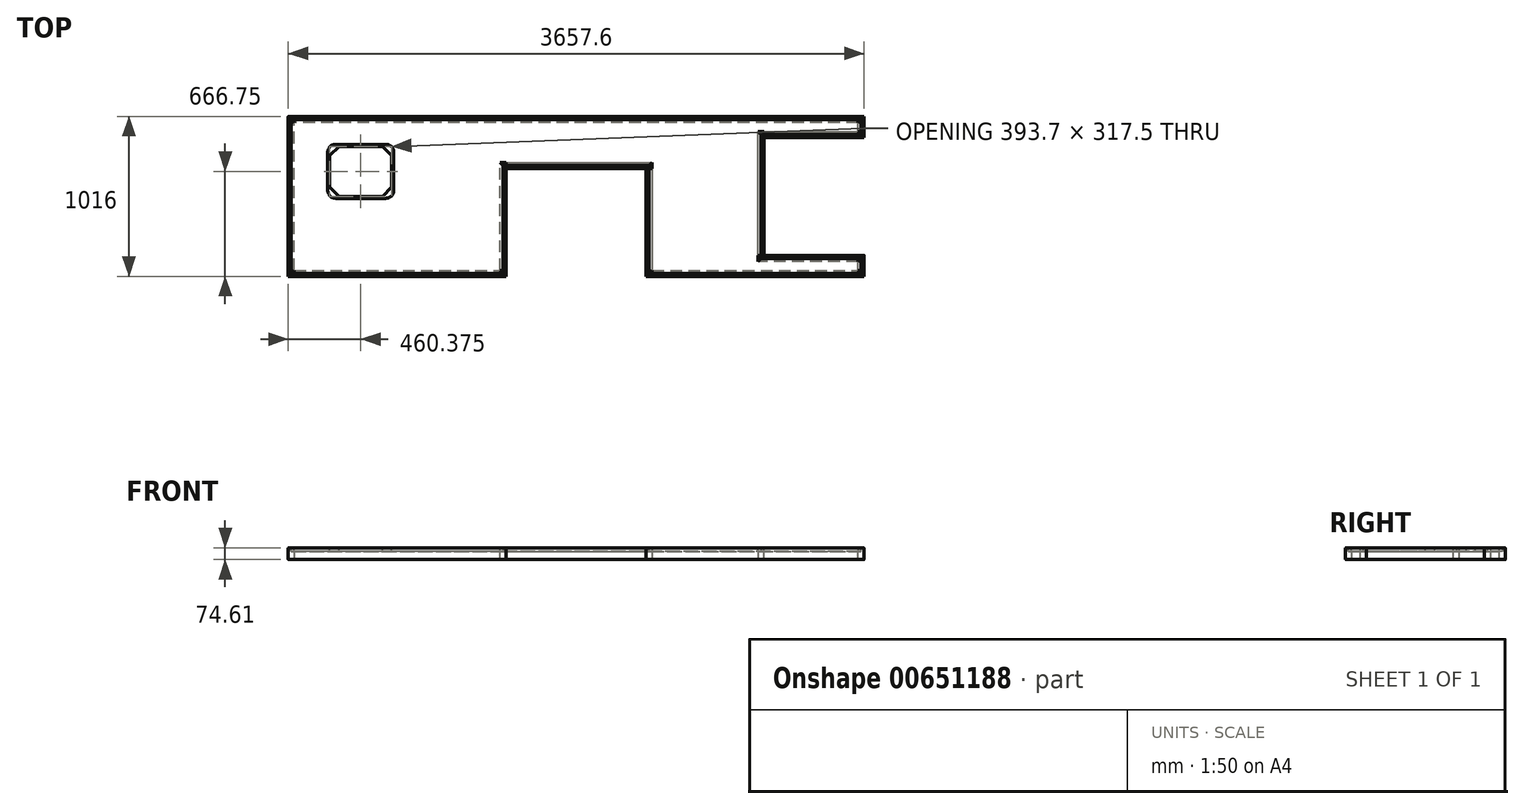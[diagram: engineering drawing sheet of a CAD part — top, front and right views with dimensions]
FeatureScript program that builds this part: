
annotation { "Feature Type Name" : "Feature", "Feature Type Description" : "" }
export const myFeature = defineFeature(function(context is Context, id is Id, definition is map)
    precondition{}
    {
        {
            var Q0;
            Q0=qCreatedBy(makeId("Top.planeOp"),FACE);
            var sketch = newSketch(context, id + "F0", { "sketchPlane" : qUnion([Q0])});
            skLineSegment(sketch, "E0.bottom", {"start": v(1809.75, 488.95) * mm, "end": v(-1809.75, 488.95) * mm});
            skLineSegment(sketch, "E0.top", {"start": v(1809.75, -488.95) * mm, "end": v(463.55, -488.95) * mm});
            skLineSegment(sketch, "E0.left", {"start": v(1809.75, 488.95) * mm, "end": v(1809.75, 393.7) * mm});
            skLineSegment(sketch, "E0.right", {"start": v(-1809.75, 488.95) * mm, "end": v(-1809.75, -488.95) * mm});
            skPoint(sketch, "E0.middle", {"position": v(0, 0) * mm});
            skLineSegment(sketch, "E1", {"start": v(-463.55, -488.95) * mm, "end": v(-463.55, 196.85) * mm});
            skLineSegment(sketch, "E2", {"start": v(-463.55, 196.85) * mm, "end": v(463.55, 196.85) * mm});
            skLineSegment(sketch, "E3", {"start": v(463.55, 196.85) * mm, "end": v(463.55, -488.95) * mm});
            skLineSegment(sketch, "E4.trimOffspring", {"start": v(-463.55, -488.95) * mm, "end": v(-1809.75, -488.95) * mm});
            skLineSegment(sketch, "E5", {"start": v(1809.75, 393.7) * mm, "end": v(1174.75, 393.7) * mm});
            skLineSegment(sketch, "E6", {"start": v(1174.75, 393.7) * mm, "end": v(1174.75, -393.7) * mm});
            skLineSegment(sketch, "E7", {"start": v(1174.75, -393.7) * mm, "end": v(1809.75, -393.7) * mm});
            skLineSegment(sketch, "E8.trimOffspring", {"start": v(1809.75, -393.7) * mm, "end": v(1809.75, -488.95) * mm});
            skSolve(sketch);
        }
        {
            var Q0;
            Q0=makeQuery(id+"F0.imprint","IMPRINT",FACE,{"disambiguationData":[TD([[makeQuery(id+"F0.imprint","IMPRINT",EDGE,{"derivedFrom":sQuery(id+"F0.wireOp",EDGE,"E0.bottom")}),1.0]])]});
            extrude(context, id + "F1", {"entities" : qUnion([Q0]), "oppositeDirection" : true, "depth" : 23.8 * mm, "offsetDistance" : 25.4 * mm});
        }
        {
            var Q0;
            Q0=qCreatedBy(makeId("Top.planeOp"),FACE);
            var sketch = newSketch(context, id + "F2", { "sketchPlane" : qUnion([Q0])});
            skLineSegment(sketch, "E9.bottom", {"start": v(-1209.68, 330.2) * mm, "end": v(-1527.18, 330.2) * mm});
            skLineSegment(sketch, "E9.top", {"start": v(-1209.68, -12.7) * mm, "end": v(-1527.18, -12.7) * mm});
            skLineSegment(sketch, "E9.left", {"start": v(-1158.88, 279.4) * mm, "end": v(-1158.88, 38.1) * mm});
            skLineSegment(sketch, "E9.right", {"start": v(-1577.98, 279.4) * mm, "end": v(-1577.98, 38.1) * mm});
            skPoint(sketch, "E10.visualSharp", {"position": v(-1577.98, 330.2) * mm});
            skArc(sketch, "E10.filletArc", {"start": v(-1527.18, 330.2) * mm, "mid": v(-1563.1, 315.32) * mm, "end": v(-1577.98, 279.4) * mm});
            skPoint(sketch, "E11.visualSharp", {"position": v(-1158.88, 330.2) * mm});
            skArc(sketch, "E11.filletArc", {"start": v(-1158.88, 279.4) * mm, "mid": v(-1173.75, 315.32) * mm, "end": v(-1209.68, 330.2) * mm});
            skPoint(sketch, "E12.visualSharp", {"position": v(-1158.88, -12.7) * mm});
            skArc(sketch, "E12.filletArc", {"start": v(-1209.68, -12.7) * mm, "mid": v(-1173.75, 2.18) * mm, "end": v(-1158.88, 38.1) * mm});
            skPoint(sketch, "E13.visualSharp", {"position": v(-1577.98, -12.7) * mm});
            skArc(sketch, "E13.filletArc", {"start": v(-1577.98, 38.1) * mm, "mid": v(-1563.1, 2.18) * mm, "end": v(-1527.18, -12.7) * mm});
            skSolve(sketch);
        }
        {
            var Q0;
            Q0=makeQuery(id+"F2.imprint","IMPRINT",FACE,{"disambiguationData":[TD([[makeQuery(id+"F2.imprint","IMPRINT",EDGE,{"derivedFrom":sQuery(id+"F2.wireOp",EDGE,"E9.bottom")}),1.0]])]});
            extrude(context, id + "F3", {"entities" : qUnion([Q0]), "operationType" : NewBodyOperationType.REMOVE, "oppositeDirection" : true, "depth" : 3 / 203.2 * mm, "offsetDistance" : 25.4 * mm});
        }
        {
            var Q0;
            Q0=qCreatedBy(makeId("Top.planeOp"),FACE);
            var sketch = newSketch(context, id + "F4", { "sketchPlane" : qUnion([Q0])});
            skPoint(sketch, "E14.0", {"position": v(-1173.75, 315.32) * mm});
            skPoint(sketch, "E15.0", {"position": v(-1158.88, 158.75) * mm});
            skPoint(sketch, "E16.0", {"position": v(-1173.75, 2.18) * mm});
            skPoint(sketch, "E17.0", {"position": v(-1368.43, -12.7) * mm});
            skPoint(sketch, "E18.0", {"position": v(-1563.1, 2.18) * mm});
            skPoint(sketch, "E19.0", {"position": v(-1577.98, 158.75) * mm});
            skPoint(sketch, "E20.0", {"position": v(-1563.1, 315.32) * mm});
            skPoint(sketch, "E21.0", {"position": v(-1368.43, 330.2) * mm});
            skLineSegment(sketch, "E22", {"start": v(-1158.88, 158.75) * mm, "end": v(-1577.98, 158.75) * mm, "construction": true});
            skLineSegment(sketch, "E23", {"start": v(-1368.43, 330.2) * mm, "end": v(-1368.43, -12.7) * mm, "construction": true});
            skLineSegment(sketch, "E24", {"start": v(-1171.58, 158.75) * mm, "end": v(-1171.58, 259.26) * mm});
            skLineSegment(sketch, "E25", {"start": v(-1171.58, 259.26) * mm, "end": v(-1229.81, 317.5) * mm});
            skLineSegment(sketch, "E26", {"start": v(-1229.81, 317.5) * mm, "end": v(-1368.43, 317.5) * mm});
            skLineSegment(sketch, "E27.MirrorCS", {"start": v(-1171.58, 158.75) * mm, "end": v(-1171.58, 58.24) * mm});
            skLineSegment(sketch, "E28.MirrorCS", {"start": v(-1171.58, 58.24) * mm, "end": v(-1229.81, 0) * mm});
            skLineSegment(sketch, "E29.MirrorCS", {"start": v(-1229.81, 0) * mm, "end": v(-1368.43, 0) * mm});
            skLineSegment(sketch, "E30.MirrorCS", {"start": v(-1507.04, 0) * mm, "end": v(-1368.43, 0) * mm});
            skLineSegment(sketch, "E31.MirrorCS", {"start": v(-1565.28, 58.24) * mm, "end": v(-1507.04, 0) * mm});
            skLineSegment(sketch, "E32.MirrorCS", {"start": v(-1565.28, 158.75) * mm, "end": v(-1565.28, 58.24) * mm});
            skLineSegment(sketch, "E33.MirrorCS", {"start": v(-1565.28, 158.75) * mm, "end": v(-1565.28, 259.26) * mm});
            skLineSegment(sketch, "E34.MirrorCS", {"start": v(-1565.28, 259.26) * mm, "end": v(-1507.04, 317.5) * mm});
            skLineSegment(sketch, "E35.MirrorCS", {"start": v(-1507.04, 317.5) * mm, "end": v(-1368.43, 317.5) * mm});
            skSolve(sketch);
        }
        {
            var Q0;
            Q0=makeQuery(id+"F4.imprint","IMPRINT",FACE,{"disambiguationData":[TD([[makeQuery(id+"F4.imprint","IMPRINT",EDGE,{"derivedFrom":sQuery(id+"F4.wireOp",EDGE,"E24")}),1.0]])]});
            extrude(context, id + "F5", {"entities" : qUnion([Q0]), "operationType" : NewBodyOperationType.REMOVE, "endBound" : BoundingType.THROUGH_ALL, "oppositeDirection" : true, "depth" : 25.4 * mm, "offsetDistance" : 25.4 * mm});
        }
        {
            var Q0;
            Q0=qCreatedBy(makeId("Front.planeOp"),FACE);
            var sketch = newSketch(context, id + "F6", { "sketchPlane" : qUnion([Q0])});
            skPoint(sketch, "E36.0", {"position": v(-1809.75, 0) * mm});
            skPoint(sketch, "E37.0", {"position": v(-1809.75, -23.81) * mm});
            skLineSegment(sketch, "E38.0", {"start": v(-1790.7, -23.81) * mm, "end": v(-1809.75, -23.81) * mm});
            skLineSegment(sketch, "E39", {"start": v(-1809.75, 0) * mm, "end": v(-1825.63, 0) * mm});
            skLineSegment(sketch, "E40", {"start": v(-1828.8, -3.17) * mm, "end": v(-1828.8, -71.44) * mm});
            skLineSegment(sketch, "E41", {"start": v(-1825.63, -74.61) * mm, "end": v(-1793.88, -74.61) * mm});
            skLineSegment(sketch, "E42", {"start": v(-1790.7, -71.44) * mm, "end": v(-1790.7, -23.81) * mm});
            skLineSegment(sketch, "E43", {"start": v(-1809.75, 0) * mm, "end": v(-1809.75, -23.81) * mm});
            skPoint(sketch, "E44.visualSharp", {"position": v(-1828.8, 0) * mm});
            skArc(sketch, "E44.filletArc", {"start": v(-1825.63, 0) * mm, "mid": v(-1827.87, -0.93) * mm, "end": v(-1828.8, -3.17) * mm});
            skPoint(sketch, "E45.visualSharp", {"position": v(-1828.8, -74.61) * mm});
            skArc(sketch, "E45.filletArc", {"start": v(-1828.8, -71.44) * mm, "mid": v(-1827.87, -73.68) * mm, "end": v(-1825.63, -74.61) * mm});
            skPoint(sketch, "E46.visualSharp", {"position": v(-1790.7, -74.61) * mm});
            skArc(sketch, "E46.filletArc", {"start": v(-1793.88, -74.61) * mm, "mid": v(-1791.63, -73.68) * mm, "end": v(-1790.7, -71.44) * mm});
            skSolve(sketch);
        }
        {
            var Q0;
            Q0 = qSketchRegion(id + "F6", true);
            extrude(context, id + "F7", {"entities" : qUnion([Q0]), "depth" : 1016 * mm, "offsetDistance" : 25.4 * mm, "symmetric" : true});
        }
        {
            var Q0;
            Q0=qCreatedBy(makeId("Top.planeOp"),FACE);
            var sketch = newSketch(context, id + "F8", { "sketchPlane" : qUnion([Q0])});
            skPoint(sketch, "E47.0", {"position": v(-1828.8, 508) * mm});
            skPoint(sketch, "E48.0", {"position": v(-1790.7, 508) * mm});
            skLineSegment(sketch, "E49", {"start": v(-1828.8, 508) * mm, "end": v(-1790.7, 508) * mm});
            skLineSegment(sketch, "E50", {"start": v(-1790.7, 469.9) * mm, "end": v(-1828.8, 508) * mm});
            skPoint(sketch, "E51.0", {"position": v(-1828.8, -508) * mm});
            skPoint(sketch, "E52.0", {"position": v(-1790.7, -508) * mm});
            skLineSegment(sketch, "E53", {"start": v(-1828.8, -508) * mm, "end": v(-1790.7, -508) * mm});
            skLineSegment(sketch, "E54", {"start": v(-1790.7, -469.9) * mm, "end": v(-1828.8, -508) * mm});
            skLineSegment(sketch, "E55", {"start": v(-1790.7, 508) * mm, "end": v(-1790.7, 469.9) * mm});
            skLineSegment(sketch, "E56", {"start": v(-1790.7, -469.9) * mm, "end": v(-1790.7, -508) * mm});
            skSolve(sketch);
        }
        {
            var Q0;
            Q0 = qSketchRegion(id + "F8", true);
            extrude(context, id + "F9", {"entities" : qUnion([Q0]), "operationType" : NewBodyOperationType.REMOVE, "endBound" : BoundingType.THROUGH_ALL, "oppositeDirection" : true, "depth" : 25.4 * mm, "offsetDistance" : 25.4 * mm});
        }
        {
            var Q0;
            Q0=makeQuery(id+"F1.opExtrude","SWEPT_FACE",FACE,{"disambiguationData":[OSD([sQuery(id+"F0.wireOp",EDGE,"E1")])]});
            var sketch = newSketch(context, id + "F10", { "sketchPlane" : qUnion([Q0])});
            skLineSegment(sketch, "E57.0", {"start": v(-488.95, -23.81) * mm, "end": v(-488.95, 0) * mm});
            skLineSegment(sketch, "E58.0", {"start": v(-469.9, -23.81) * mm, "end": v(-488.95, -23.81) * mm});
            skLineSegment(sketch, "E59", {"start": v(-488.95, 0) * mm, "end": v(-504.83, 0) * mm});
            skLineSegment(sketch, "E60", {"start": v(-508, -3.17) * mm, "end": v(-508, -71.44) * mm});
            skLineSegment(sketch, "E61", {"start": v(-504.83, -74.61) * mm, "end": v(-473.08, -74.61) * mm});
            skLineSegment(sketch, "E62", {"start": v(-469.9, -71.44) * mm, "end": v(-469.9, -23.81) * mm});
            skPoint(sketch, "E63.visualSharp", {"position": v(-508, 0) * mm});
            skArc(sketch, "E63.filletArc", {"start": v(-504.83, 0) * mm, "mid": v(-507.07, -0.93) * mm, "end": v(-508, -3.18) * mm});
            skPoint(sketch, "E64.visualSharp", {"position": v(-508, -74.61) * mm});
            skArc(sketch, "E64.filletArc", {"start": v(-508, -71.44) * mm, "mid": v(-507.07, -73.68) * mm, "end": v(-504.83, -74.61) * mm});
            skPoint(sketch, "E65.visualSharp", {"position": v(-469.9, -74.61) * mm});
            skArc(sketch, "E65.filletArc", {"start": v(-473.08, -74.61) * mm, "mid": v(-470.83, -73.68) * mm, "end": v(-469.9, -71.44) * mm});
            skSolve(sketch);
        }
        {
            var Q0;
            Q0 = qSketchRegion(id + "F10", true);
            extrude(context, id + "F11", {"entities" : qUnion([Q0]), "endBound" : BoundingType.UP_TO_NEXT, "oppositeDirection" : true, "depth" : 25.4 * mm, "offsetDistance" : 25.4 * mm, "hasSecondDirection" : true, "secondDirectionOppositeDirection" : false, "secondDirectionDepth" : 19.05 * mm});
        }
        {
            var Q0;
            Q0=qCreatedBy(makeId("Top.planeOp"),FACE);
            var sketch = newSketch(context, id + "F12", { "sketchPlane" : qUnion([Q0])});
            skPoint(sketch, "E66.0", {"position": v(-444.5, -508) * mm});
            skPoint(sketch, "E67.0", {"position": v(-444.5, -469.9) * mm});
            skLineSegment(sketch, "E68", {"start": v(-444.5, -508) * mm, "end": v(-444.5, -469.9) * mm});
            skLineSegment(sketch, "E69", {"start": v(-444.5, -469.9) * mm, "end": v(-482.6, -469.9) * mm});
            skLineSegment(sketch, "E70", {"start": v(-482.6, -469.9) * mm, "end": v(-444.5, -508) * mm});
            skSolve(sketch);
        }
        {
            var Q0;
            Q0 = qSketchRegion(id + "F12", true);
            extrude(context, id + "F13", {"entities" : qUnion([Q0]), "operationType" : NewBodyOperationType.REMOVE, "endBound" : BoundingType.THROUGH_ALL, "oppositeDirection" : true, "depth" : 25.4 * mm, "offsetDistance" : 25.4 * mm});
        }
        {
            var Q0;
            Q0=makeQuery(id+"F1.opExtrude","SWEPT_FACE",FACE,{"disambiguationData":[OSD([sQuery(id+"F0.wireOp",EDGE,"E2")])]});
            var sketch = newSketch(context, id + "F14", { "sketchPlane" : qUnion([Q0])});
            skLineSegment(sketch, "E71.0", {"start": v(-463.55, -23.81) * mm, "end": v(-463.55, 0) * mm});
            skLineSegment(sketch, "E72", {"start": v(-463.55, 0) * mm, "end": v(-447.68, 0) * mm});
            skLineSegment(sketch, "E73", {"start": v(-444.5, -3.17) * mm, "end": v(-444.5, -71.44) * mm});
            skLineSegment(sketch, "E74", {"start": v(-447.68, -74.61) * mm, "end": v(-479.43, -74.61) * mm});
            skLineSegment(sketch, "E75", {"start": v(-463.55, -23.81) * mm, "end": v(-482.6, -23.81) * mm});
            skLineSegment(sketch, "E76", {"start": v(-482.6, -23.81) * mm, "end": v(-482.6, -71.44) * mm});
            skPoint(sketch, "E77.visualSharp", {"position": v(-444.5, 0) * mm});
            skArc(sketch, "E77.filletArc", {"start": v(-444.5, -3.17) * mm, "mid": v(-445.43, -0.93) * mm, "end": v(-447.68, 0) * mm});
            skPoint(sketch, "E78.visualSharp", {"position": v(-444.5, -74.61) * mm});
            skArc(sketch, "E78.filletArc", {"start": v(-447.68, -74.61) * mm, "mid": v(-445.43, -73.68) * mm, "end": v(-444.5, -71.44) * mm});
            skPoint(sketch, "E79.visualSharp", {"position": v(-482.6, -74.61) * mm});
            skArc(sketch, "E79.filletArc", {"start": v(-482.6, -71.44) * mm, "mid": v(-481.67, -73.68) * mm, "end": v(-479.43, -74.61) * mm});
            skSolve(sketch);
        }
        {
            var Q0;
            Q0 = qSketchRegion(id + "F14", true);
            extrude(context, id + "F15", {"entities" : qUnion([Q0]), "endBound" : BoundingType.UP_TO_NEXT, "depth" : 25.4 * mm, "offsetDistance" : 25.4 * mm, "hasSecondDirection" : true, "secondDirectionOppositeDirection" : true, "secondDirectionDepth" : 19.05 * mm});
        }
        {
            var Q0;
            Q0=qCreatedBy(makeId("Top.planeOp"),FACE);
            var sketch = newSketch(context, id + "F16", { "sketchPlane" : qUnion([Q0])});
            skPoint(sketch, "E80.0", {"position": v(-482.6, 215.9) * mm});
            skPoint(sketch, "E81.0", {"position": v(-444.5, 215.9) * mm});
            skLineSegment(sketch, "E82", {"start": v(-482.6, 215.9) * mm, "end": v(-444.5, 215.9) * mm});
            skLineSegment(sketch, "E83", {"start": v(-444.5, 215.9) * mm, "end": v(-444.5, 177.8) * mm});
            skLineSegment(sketch, "E84", {"start": v(-444.5, 177.8) * mm, "end": v(-482.6, 215.9) * mm});
            skSolve(sketch);
        }
        {
            var Q0;
            Q0 = qSketchRegion(id + "F16", true);
            extrude(context, id + "F17", {"entities" : qUnion([Q0]), "operationType" : NewBodyOperationType.REMOVE, "endBound" : BoundingType.THROUGH_ALL, "oppositeDirection" : true, "depth" : 25.4 * mm, "offsetDistance" : 25.4 * mm});
        }
        {
            var Q0;
            Q0=makeQuery(id+"F1.opExtrude","SWEPT_FACE",FACE,{"disambiguationData":[OSD([sQuery(id+"F0.wireOp",EDGE,"E3")])]});
            var sketch = newSketch(context, id + "F18", { "sketchPlane" : qUnion([Q0])});
            skLineSegment(sketch, "E85.0", {"start": v(-196.85, -23.81) * mm, "end": v(-196.85, 0) * mm});
            skLineSegment(sketch, "E86", {"start": v(-196.85, 0) * mm, "end": v(-180.97, 0) * mm});
            skLineSegment(sketch, "E87", {"start": v(-177.8, -3.17) * mm, "end": v(-177.8, -71.44) * mm});
            skLineSegment(sketch, "E88", {"start": v(-180.97, -74.61) * mm, "end": v(-212.72, -74.61) * mm});
            skLineSegment(sketch, "E89", {"start": v(-196.85, -23.81) * mm, "end": v(-215.9, -23.81) * mm});
            skLineSegment(sketch, "E90", {"start": v(-215.9, -23.81) * mm, "end": v(-215.9, -71.44) * mm});
            skPoint(sketch, "E91.visualSharp", {"position": v(-177.8, 0) * mm});
            skArc(sketch, "E91.filletArc", {"start": v(-177.8, -3.18) * mm, "mid": v(-178.73, -0.93) * mm, "end": v(-180.97, 0) * mm});
            skPoint(sketch, "E92.visualSharp", {"position": v(-177.8, -74.61) * mm});
            skArc(sketch, "E92.filletArc", {"start": v(-180.97, -74.61) * mm, "mid": v(-178.73, -73.68) * mm, "end": v(-177.8, -71.44) * mm});
            skPoint(sketch, "E93.visualSharp", {"position": v(-215.9, -74.61) * mm});
            skArc(sketch, "E93.filletArc", {"start": v(-215.9, -71.44) * mm, "mid": v(-214.97, -73.68) * mm, "end": v(-212.72, -74.61) * mm});
            skSolve(sketch);
        }
        {
            var Q0;
            Q0 = qSketchRegion(id + "F18", true);
            extrude(context, id + "F19", {"entities" : qUnion([Q0]), "endBound" : BoundingType.UP_TO_NEXT, "depth" : 25.4 * mm, "offsetDistance" : 25.4 * mm, "hasSecondDirection" : true, "secondDirectionOppositeDirection" : true, "secondDirectionDepth" : 19.05 * mm});
        }
        {
            var Q0;
            Q0=qCreatedBy(makeId("Top.planeOp"),FACE);
            var sketch = newSketch(context, id + "F20", { "sketchPlane" : qUnion([Q0])});
            skPoint(sketch, "E94.0", {"position": v(482.6, 177.8) * mm});
            skPoint(sketch, "E95.0", {"position": v(482.6, 215.9) * mm});
            skLineSegment(sketch, "E96", {"start": v(482.6, 177.8) * mm, "end": v(482.6, 215.9) * mm});
            skLineSegment(sketch, "E97", {"start": v(482.6, 215.9) * mm, "end": v(444.5, 177.8) * mm});
            skLineSegment(sketch, "E98", {"start": v(444.5, 177.8) * mm, "end": v(482.6, 177.8) * mm});
            skSolve(sketch);
        }
        {
            var Q0;
            Q0 = qSketchRegion(id + "F20", true);
            extrude(context, id + "F21", {"entities" : qUnion([Q0]), "operationType" : NewBodyOperationType.REMOVE, "endBound" : BoundingType.THROUGH_ALL, "oppositeDirection" : true, "depth" : 25.4 * mm, "offsetDistance" : 25.4 * mm});
        }
        {
            var Q0;
            Q0=makeQuery(id+"F1.opExtrude","SWEPT_FACE",FACE,{"disambiguationData":[OSD([sQuery(id+"F0.wireOp",EDGE,"E0.top")])]});
            var sketch = newSketch(context, id + "F22", { "sketchPlane" : qUnion([Q0])});
            skLineSegment(sketch, "E99.0", {"start": v(463.55, -23.81) * mm, "end": v(463.55, 0) * mm});
            skLineSegment(sketch, "E100", {"start": v(463.55, 0) * mm, "end": v(447.67, 0) * mm});
            skLineSegment(sketch, "E101", {"start": v(444.5, -3.17) * mm, "end": v(444.5, -71.44) * mm});
            skLineSegment(sketch, "E102", {"start": v(447.67, -74.61) * mm, "end": v(479.42, -74.61) * mm});
            skLineSegment(sketch, "E103", {"start": v(482.6, -71.44) * mm, "end": v(482.6, -23.81) * mm});
            skLineSegment(sketch, "E104", {"start": v(482.6, -23.81) * mm, "end": v(463.55, -23.81) * mm});
            skPoint(sketch, "E105.visualSharp", {"position": v(444.5, 0) * mm});
            skArc(sketch, "E105.filletArc", {"start": v(447.67, 0) * mm, "mid": v(445.43, -0.93) * mm, "end": v(444.5, -3.17) * mm});
            skPoint(sketch, "E106.visualSharp", {"position": v(444.5, -74.61) * mm});
            skArc(sketch, "E106.filletArc", {"start": v(444.5, -71.44) * mm, "mid": v(445.43, -73.68) * mm, "end": v(447.67, -74.61) * mm});
            skPoint(sketch, "E107.visualSharp", {"position": v(482.6, -74.61) * mm});
            skArc(sketch, "E107.filletArc", {"start": v(479.42, -74.61) * mm, "mid": v(481.67, -73.68) * mm, "end": v(482.6, -71.44) * mm});
            skSolve(sketch);
        }
        {
            var Q0;
            Q0 = qSketchRegion(id + "F22", true);
            extrude(context, id + "F23", {"entities" : qUnion([Q0]), "endBound" : BoundingType.UP_TO_NEXT, "oppositeDirection" : true, "depth" : 25.4 * mm, "offsetDistance" : 25.4 * mm, "hasSecondDirection" : true, "secondDirectionOppositeDirection" : false, "secondDirectionDepth" : 19.05 * mm});
        }
        {
            var Q0;
            Q0=qCreatedBy(makeId("Top.planeOp"),FACE);
            var sketch = newSketch(context, id + "F24", { "sketchPlane" : qUnion([Q0])});
            skPoint(sketch, "E108.0", {"position": v(444.5, -508) * mm});
            skPoint(sketch, "E109.0", {"position": v(482.6, -508) * mm});
            skLineSegment(sketch, "E110", {"start": v(444.5, -508) * mm, "end": v(482.6, -508) * mm});
            skLineSegment(sketch, "E111", {"start": v(482.6, -508) * mm, "end": v(482.6, -469.9) * mm});
            skLineSegment(sketch, "E112", {"start": v(482.6, -469.9) * mm, "end": v(444.5, -508) * mm});
            skSolve(sketch);
        }
        {
            var Q0;
            Q0 = qSketchRegion(id + "F24", true);
            extrude(context, id + "F25", {"entities" : qUnion([Q0]), "operationType" : NewBodyOperationType.REMOVE, "endBound" : BoundingType.THROUGH_ALL, "oppositeDirection" : true, "depth" : 25.4 * mm, "offsetDistance" : 25.4 * mm});
        }
        {
            var Q0;
            Q0=makeQuery(id+"F1.opExtrude","SWEPT_FACE",FACE,{"disambiguationData":[OSD([sQuery(id+"F0.wireOp",EDGE,"E8.trimOffspring")])]});
            var sketch = newSketch(context, id + "F26", { "sketchPlane" : qUnion([Q0])});
            skLineSegment(sketch, "E113.0", {"start": v(-488.95, -23.81) * mm, "end": v(-488.95, 0) * mm});
            skLineSegment(sketch, "E114.0.0", {"start": v(-469.9, -23.81) * mm, "end": v(-488.95, -23.81) * mm});
            skLineSegment(sketch, "E114.0.2", {"start": v(-488.95, 0) * mm, "end": v(-504.82, 0) * mm});
            skArc(sketch, "E114.0.3", {"start": v(-504.82, 0) * mm, "mid": v(-507.07, -0.93) * mm, "end": v(-508, -3.17) * mm});
            skLineSegment(sketch, "E114.0.4", {"start": v(-508, -3.17) * mm, "end": v(-508, -71.44) * mm});
            skArc(sketch, "E114.0.5", {"start": v(-508, -71.44) * mm, "mid": v(-507.07, -73.68) * mm, "end": v(-504.82, -74.61) * mm});
            skLineSegment(sketch, "E114.0.6", {"start": v(-504.82, -74.61) * mm, "end": v(-473.07, -74.61) * mm});
            skArc(sketch, "E114.0.7", {"start": v(-473.07, -74.61) * mm, "mid": v(-470.83, -73.68) * mm, "end": v(-469.9, -71.44) * mm});
            skLineSegment(sketch, "E114.0.8", {"start": v(-469.9, -71.44) * mm, "end": v(-469.9, -23.81) * mm});
            skSolve(sketch);
        }
        {
            var Q0;
            Q0=makeQuery(id+"F26.imprint","IMPRINT",FACE,{"disambiguationData":[TD([[makeQuery(id+"F26.imprint","IMPRINT",EDGE,{"derivedFrom":sQuery(id+"F26.wireOp",EDGE,"E114.0.0")}),1.0]])]});
            extrude(context, id + "F27", {"entities" : qUnion([Q0]), "endBound" : BoundingType.UP_TO_NEXT, "oppositeDirection" : true, "depth" : 25.4 * mm, "offsetDistance" : 25.4 * mm, "hasSecondDirection" : true, "secondDirectionOppositeDirection" : false, "secondDirectionDepth" : 19.05 * mm});
        }
        {
            var Q0;
            Q0=qCreatedBy(makeId("Top.planeOp"),FACE);
            var sketch = newSketch(context, id + "F28", { "sketchPlane" : qUnion([Q0])});
            skPoint(sketch, "E115.0", {"position": v(1828.8, -469.9) * mm});
            skPoint(sketch, "E116.0", {"position": v(1828.8, -508) * mm});
            skLineSegment(sketch, "E117", {"start": v(1828.8, -508) * mm, "end": v(1828.8, -469.9) * mm});
            skLineSegment(sketch, "E118", {"start": v(1828.8, -469.9) * mm, "end": v(1790.7, -469.9) * mm});
            skLineSegment(sketch, "E119", {"start": v(1790.7, -469.9) * mm, "end": v(1828.8, -508) * mm});
            skSolve(sketch);
        }
        {
            var Q0;
            Q0 = qSketchRegion(id + "F28", true);
            extrude(context, id + "F29", {"entities" : qUnion([Q0]), "operationType" : NewBodyOperationType.REMOVE, "endBound" : BoundingType.THROUGH_ALL, "oppositeDirection" : true, "depth" : 25.4 * mm, "offsetDistance" : 25.4 * mm});
        }
        {
            var Q0;
            Q0=makeQuery(id+"F1.opExtrude","SWEPT_FACE",FACE,{"disambiguationData":[OSD([sQuery(id+"F0.wireOp",EDGE,"E7")])]});
            var sketch = newSketch(context, id + "F30", { "sketchPlane" : qUnion([Q0])});
            skLineSegment(sketch, "E120.0.0", {"start": v(-1790.7, -23.81) * mm, "end": v(-1809.75, -23.81) * mm});
            skLineSegment(sketch, "E120.0.1", {"start": v(-1809.75, -23.81) * mm, "end": v(-1809.75, 0) * mm});
            skLineSegment(sketch, "E120.0.2", {"start": v(-1809.75, 0) * mm, "end": v(-1825.62, 0) * mm});
            skArc(sketch, "E120.0.3", {"start": v(-1825.62, 0) * mm, "mid": v(-1827.87, -0.93) * mm, "end": v(-1828.8, -3.17) * mm});
            skLineSegment(sketch, "E120.0.4", {"start": v(-1828.8, -3.17) * mm, "end": v(-1828.8, -71.44) * mm});
            skArc(sketch, "E120.0.5", {"start": v(-1828.8, -71.44) * mm, "mid": v(-1827.87, -73.68) * mm, "end": v(-1825.62, -74.61) * mm});
            skLineSegment(sketch, "E120.0.6", {"start": v(-1825.62, -74.61) * mm, "end": v(-1793.87, -74.61) * mm});
            skArc(sketch, "E120.0.7", {"start": v(-1793.87, -74.61) * mm, "mid": v(-1791.63, -73.68) * mm, "end": v(-1790.7, -71.44) * mm});
            skLineSegment(sketch, "E120.0.8", {"start": v(-1790.7, -71.44) * mm, "end": v(-1790.7, -23.81) * mm});
            skSolve(sketch);
        }
        {
            var Q0;
            Q0=makeQuery(id+"F30.imprint","IMPRINT",FACE,{"disambiguationData":[TD([[makeQuery(id+"F30.imprint","IMPRINT",EDGE,{"derivedFrom":sQuery(id+"F30.wireOp",EDGE,"E120.0.0")}),1.0]])]});
            extrude(context, id + "F31", {"entities" : qUnion([Q0]), "endBound" : BoundingType.UP_TO_NEXT, "oppositeDirection" : true, "depth" : 25.4 * mm, "offsetDistance" : 25.4 * mm, "hasSecondDirection" : true, "secondDirectionOppositeDirection" : false, "secondDirectionDepth" : 19.05 * mm});
        }
        {
            var Q0;
            Q0=qCreatedBy(makeId("Top.planeOp"),FACE);
            var sketch = newSketch(context, id + "F32", { "sketchPlane" : qUnion([Q0])});
            skPoint(sketch, "E121.0", {"position": v(1828.8, -374.65) * mm});
            skPoint(sketch, "E122.0", {"position": v(1790.7, -374.65) * mm});
            skLineSegment(sketch, "E123", {"start": v(1828.8, -374.65) * mm, "end": v(1790.7, -374.65) * mm});
            skLineSegment(sketch, "E124", {"start": v(1790.7, -412.75) * mm, "end": v(1828.8, -374.65) * mm});
            skLineSegment(sketch, "E125", {"start": v(1790.7, -374.65) * mm, "end": v(1790.7, -412.75) * mm});
            skSolve(sketch);
        }
        {
            var Q0;
            Q0 = qSketchRegion(id + "F32", true);
            extrude(context, id + "F33", {"entities" : qUnion([Q0]), "operationType" : NewBodyOperationType.REMOVE, "endBound" : BoundingType.THROUGH_ALL, "oppositeDirection" : true, "depth" : 25.4 * mm, "offsetDistance" : 25.4 * mm});
        }
        {
            var Q0;
            Q0=makeQuery(id+"F1.opExtrude","SWEPT_FACE",FACE,{"disambiguationData":[OSD([sQuery(id+"F0.wireOp",EDGE,"E6")])]});
            var sketch = newSketch(context, id + "F34", { "sketchPlane" : qUnion([Q0])});
            skLineSegment(sketch, "E126.0.0", {"start": v(-412.75, -23.81) * mm, "end": v(-393.7, -23.81) * mm});
            skLineSegment(sketch, "E126.0.1", {"start": v(-393.7, -23.81) * mm, "end": v(-393.7, 0) * mm});
            skLineSegment(sketch, "E126.0.2", {"start": v(-393.7, 0) * mm, "end": v(-377.83, 0) * mm});
            skArc(sketch, "E126.0.3", {"start": v(-377.83, 0) * mm, "mid": v(-375.58, -0.93) * mm, "end": v(-374.65, -3.17) * mm});
            skLineSegment(sketch, "E126.0.4", {"start": v(-374.65, -3.17) * mm, "end": v(-374.65, -71.44) * mm});
            skArc(sketch, "E126.0.5", {"start": v(-374.65, -71.44) * mm, "mid": v(-375.58, -73.68) * mm, "end": v(-377.83, -74.61) * mm});
            skLineSegment(sketch, "E126.0.6", {"start": v(-377.83, -74.61) * mm, "end": v(-409.58, -74.61) * mm});
            skArc(sketch, "E126.0.7", {"start": v(-409.58, -74.61) * mm, "mid": v(-411.82, -73.68) * mm, "end": v(-412.75, -71.44) * mm});
            skLineSegment(sketch, "E126.0.8", {"start": v(-412.75, -71.44) * mm, "end": v(-412.75, -23.81) * mm});
            skSolve(sketch);
        }
        {
            var Q0;
            Q0 = qSketchRegion(id + "F34", true);
            extrude(context, id + "F35", {"entities" : qUnion([Q0]), "endBound" : BoundingType.UP_TO_NEXT, "depth" : 25.4 * mm, "offsetDistance" : 25.4 * mm, "hasSecondDirection" : true, "secondDirectionOppositeDirection" : true, "secondDirectionDepth" : 19.05 * mm});
        }
        {
            var Q0;
            Q0=qCreatedBy(makeId("Top.planeOp"),FACE);
            var sketch = newSketch(context, id + "F36", { "sketchPlane" : qUnion([Q0])});
            skPoint(sketch, "E127.0", {"position": v(1155.7, -412.75) * mm});
            skPoint(sketch, "E128.0", {"position": v(1155.7, -374.65) * mm});
            skLineSegment(sketch, "E129", {"start": v(1155.7, -374.65) * mm, "end": v(1193.8, -374.65) * mm});
            skLineSegment(sketch, "E130", {"start": v(1193.8, -374.65) * mm, "end": v(1155.7, -412.75) * mm});
            skLineSegment(sketch, "E131", {"start": v(1155.7, -412.75) * mm, "end": v(1155.7, -374.65) * mm});
            skSolve(sketch);
        }
        {
            var Q0;
            Q0 = qSketchRegion(id + "F36", true);
            extrude(context, id + "F37", {"entities" : qUnion([Q0]), "operationType" : NewBodyOperationType.REMOVE, "endBound" : BoundingType.THROUGH_ALL, "oppositeDirection" : true, "depth" : 25.4 * mm, "offsetDistance" : 25.4 * mm});
        }
        {
            var Q0;
            Q0=makeQuery(id+"F1.opExtrude","SWEPT_FACE",FACE,{"disambiguationData":[OSD([sQuery(id+"F0.wireOp",EDGE,"E5")])]});
            var sketch = newSketch(context, id + "F38", { "sketchPlane" : qUnion([Q0])});
            skLineSegment(sketch, "E132.0.0", {"start": v(1193.8, -3.18) * mm, "end": v(1193.8, -71.44) * mm});
            skArc(sketch, "E132.0.1", {"start": v(1190.62, -74.61) * mm, "mid": v(1192.87, -73.68) * mm, "end": v(1193.8, -71.44) * mm});
            skLineSegment(sketch, "E132.0.2", {"start": v(1190.62, -74.61) * mm, "end": v(1158.87, -74.61) * mm});
            skArc(sketch, "E132.0.3", {"start": v(1155.7, -71.44) * mm, "mid": v(1156.63, -73.68) * mm, "end": v(1158.87, -74.61) * mm});
            skLineSegment(sketch, "E132.0.4", {"start": v(1155.7, -71.44) * mm, "end": v(1155.7, -23.81) * mm});
            skLineSegment(sketch, "E132.0.5", {"start": v(1155.7, -23.81) * mm, "end": v(1174.75, -23.81) * mm});
            skLineSegment(sketch, "E132.0.6", {"start": v(1174.75, -23.81) * mm, "end": v(1174.75, 0) * mm});
            skLineSegment(sketch, "E132.0.7", {"start": v(1174.75, 0) * mm, "end": v(1190.62, 0) * mm});
            skArc(sketch, "E132.0.8", {"start": v(1193.8, -3.18) * mm, "mid": v(1192.87, -0.93) * mm, "end": v(1190.62, 0) * mm});
            skSolve(sketch);
        }
        {
            var Q0;
            Q0 = qSketchRegion(id + "F38", true);
            extrude(context, id + "F39", {"entities" : qUnion([Q0]), "endBound" : BoundingType.UP_TO_NEXT, "depth" : 25.4 * mm, "offsetDistance" : 25.4 * mm, "hasSecondDirection" : true, "secondDirectionOppositeDirection" : true, "secondDirectionDepth" : 19.05 * mm});
        }
        {
            var Q0;
            Q0=qCreatedBy(makeId("Top.planeOp"),FACE);
            var sketch = newSketch(context, id + "F40", { "sketchPlane" : qUnion([Q0])});
            skPoint(sketch, "E133.0", {"position": v(1155.7, 412.75) * mm});
            skPoint(sketch, "E134.0", {"position": v(1193.8, 412.75) * mm});
            skLineSegment(sketch, "E135", {"start": v(1155.7, 412.75) * mm, "end": v(1193.8, 412.75) * mm});
            skLineSegment(sketch, "E136", {"start": v(1193.8, 412.75) * mm, "end": v(1193.8, 374.65) * mm});
            skLineSegment(sketch, "E137", {"start": v(1193.8, 374.65) * mm, "end": v(1155.7, 412.75) * mm});
            skSolve(sketch);
        }
        {
            var Q0;
            Q0 = qSketchRegion(id + "F40", true);
            extrude(context, id + "F41", {"entities" : qUnion([Q0]), "operationType" : NewBodyOperationType.REMOVE, "endBound" : BoundingType.THROUGH_ALL, "oppositeDirection" : true, "depth" : 25.4 * mm, "offsetDistance" : 25.4 * mm});
        }
        {
            var Q0;
            Q0=makeQuery(id+"F1.opExtrude","SWEPT_FACE",FACE,{"disambiguationData":[OSD([sQuery(id+"F0.wireOp",EDGE,"E0.left")])]});
            var sketch = newSketch(context, id + "F42", { "sketchPlane" : qUnion([Q0])});
            skArc(sketch, "E138.0.0", {"start": v(409.58, -74.61) * mm, "mid": v(411.82, -73.68) * mm, "end": v(412.75, -71.44) * mm});
            skLineSegment(sketch, "E138.0.1", {"start": v(412.75, -71.44) * mm, "end": v(412.75, -23.81) * mm});
            skLineSegment(sketch, "E138.0.2", {"start": v(412.75, -23.81) * mm, "end": v(393.7, -23.81) * mm});
            skLineSegment(sketch, "E138.0.3", {"start": v(393.7, -23.81) * mm, "end": v(393.7, 0) * mm});
            skLineSegment(sketch, "E138.0.4", {"start": v(393.7, 0) * mm, "end": v(377.83, 0) * mm});
            skArc(sketch, "E138.0.5", {"start": v(377.83, 0) * mm, "mid": v(375.58, -0.93) * mm, "end": v(374.65, -3.18) * mm});
            skLineSegment(sketch, "E138.0.6", {"start": v(374.65, -3.18) * mm, "end": v(374.65, -71.44) * mm});
            skArc(sketch, "E138.0.7", {"start": v(374.65, -71.44) * mm, "mid": v(375.58, -73.68) * mm, "end": v(377.83, -74.61) * mm});
            skLineSegment(sketch, "E138.0.8", {"start": v(377.83, -74.61) * mm, "end": v(409.58, -74.61) * mm});
            skSolve(sketch);
        }
        {
            var Q0;
            Q0 = qSketchRegion(id + "F42", true);
            extrude(context, id + "F43", {"entities" : qUnion([Q0]), "endBound" : BoundingType.UP_TO_NEXT, "oppositeDirection" : true, "depth" : 25.4 * mm, "offsetDistance" : 25.4 * mm, "hasSecondDirection" : true, "secondDirectionOppositeDirection" : false, "secondDirectionDepth" : 19.05 * mm});
        }
        {
            var Q0;
            Q0=qCreatedBy(makeId("Top.planeOp"),FACE);
            var sketch = newSketch(context, id + "F44", { "sketchPlane" : qUnion([Q0])});
            skPoint(sketch, "E139.0", {"position": v(1828.8, 374.65) * mm});
            skPoint(sketch, "E140.0", {"position": v(1828.8, 412.75) * mm});
            skLineSegment(sketch, "E141", {"start": v(1828.8, 374.65) * mm, "end": v(1828.8, 412.75) * mm});
            skLineSegment(sketch, "E142", {"start": v(1828.8, 412.75) * mm, "end": v(1790.7, 412.75) * mm});
            skLineSegment(sketch, "E143", {"start": v(1790.7, 412.75) * mm, "end": v(1828.8, 374.65) * mm});
            skSolve(sketch);
        }
        {
            var Q0;
            Q0 = qSketchRegion(id + "F44", true);
            extrude(context, id + "F45", {"entities" : qUnion([Q0]), "operationType" : NewBodyOperationType.REMOVE, "endBound" : BoundingType.THROUGH_ALL, "oppositeDirection" : true, "depth" : 25.4 * mm, "offsetDistance" : 25.4 * mm});
        }
        {
            var Q0;
            Q0=makeQuery(id+"F1.opExtrude","SWEPT_FACE",FACE,{"disambiguationData":[OSD([sQuery(id+"F0.wireOp",EDGE,"E0.bottom")])]});
            var sketch = newSketch(context, id + "F46", { "sketchPlane" : qUnion([Q0])});
            skArc(sketch, "E144.0.0", {"start": v(-1825.63, 0) * mm, "mid": v(-1827.87, -0.93) * mm, "end": v(-1828.8, -3.17) * mm});
            skLineSegment(sketch, "E144.0.1", {"start": v(-1828.8, -3.18) * mm, "end": v(-1828.8, -71.44) * mm});
            skArc(sketch, "E144.0.2", {"start": v(-1828.8, -71.44) * mm, "mid": v(-1827.87, -73.68) * mm, "end": v(-1825.63, -74.61) * mm});
            skLineSegment(sketch, "E144.0.3", {"start": v(-1825.63, -74.61) * mm, "end": v(-1793.87, -74.61) * mm});
            skArc(sketch, "E144.0.4", {"start": v(-1793.88, -74.61) * mm, "mid": v(-1791.63, -73.68) * mm, "end": v(-1790.7, -71.44) * mm});
            skLineSegment(sketch, "E144.0.5", {"start": v(-1790.7, -71.44) * mm, "end": v(-1790.7, -23.81) * mm});
            skLineSegment(sketch, "E144.0.6", {"start": v(-1790.7, -23.81) * mm, "end": v(-1809.75, -23.81) * mm});
            skLineSegment(sketch, "E144.0.7", {"start": v(-1809.75, -23.81) * mm, "end": v(-1809.75, 0) * mm});
            skLineSegment(sketch, "E144.0.8", {"start": v(-1809.75, 0) * mm, "end": v(-1825.63, 0) * mm});
            skSolve(sketch);
        }
        {
            var Q0;
            Q0=makeQuery(id+"F46.imprint","IMPRINT",FACE,{"disambiguationData":[TD([[makeQuery(id+"F46.imprint","IMPRINT",EDGE,{"derivedFrom":sQuery(id+"F46.wireOp",EDGE,"E144.0.0")}),1.0]])]});
            extrude(context, id + "F47", {"entities" : qUnion([Q0]), "endBound" : BoundingType.UP_TO_NEXT, "oppositeDirection" : true, "depth" : 25.4 * mm, "offsetDistance" : 25.4 * mm, "hasSecondDirection" : true, "secondDirectionOppositeDirection" : false, "secondDirectionDepth" : 19.05 * mm});
        }
        {
            var Q0;
            Q0=qCreatedBy(makeId("Top.planeOp"),FACE);
            var sketch = newSketch(context, id + "F48", { "sketchPlane" : qUnion([Q0])});
            skPoint(sketch, "E145.0", {"position": v(1790.7, 508) * mm});
            skPoint(sketch, "E146.0", {"position": v(1828.8, 508) * mm});
            skLineSegment(sketch, "E147", {"start": v(1828.8, 508) * mm, "end": v(1790.7, 469.9) * mm});
            skLineSegment(sketch, "E148", {"start": v(1790.7, 469.9) * mm, "end": v(1790.7, 508) * mm});
            skLineSegment(sketch, "E149", {"start": v(1790.7, 508) * mm, "end": v(1828.8, 508) * mm});
            skSolve(sketch);
        }
        {
            var Q0;
            Q0 = qSketchRegion(id + "F48", true);
            extrude(context, id + "F49", {"entities" : qUnion([Q0]), "operationType" : NewBodyOperationType.REMOVE, "endBound" : BoundingType.THROUGH_ALL, "oppositeDirection" : true, "depth" : 25.4 * mm, "offsetDistance" : 25.4 * mm});
        }
        {
            var Q0;
            Q0=qCreatedBy(makeId("Right.planeOp"),FACE);
            var sketch = newSketch(context, id + "F50", { "sketchPlane" : qUnion([Q0])});
            skLineSegment(sketch, "E150.0.0", {"start": v(488.95, -23.81) * mm, "end": v(469.9, -23.81) * mm});
            skLineSegment(sketch, "E150.0.1", {"start": v(469.9, -23.81) * mm, "end": v(469.9, -71.44) * mm});
            skArc(sketch, "E150.0.2", {"start": v(469.9, -71.44) * mm, "mid": v(470.83, -73.68) * mm, "end": v(473.07, -74.61) * mm});
            skLineSegment(sketch, "E150.0.3", {"start": v(473.07, -74.61) * mm, "end": v(504.83, -74.61) * mm});
            skArc(sketch, "E150.0.4", {"start": v(504.83, -74.61) * mm, "mid": v(507.07, -73.68) * mm, "end": v(508, -71.44) * mm});
            skLineSegment(sketch, "E150.0.5", {"start": v(508, -71.44) * mm, "end": v(508, -3.17) * mm});
            skArc(sketch, "E150.0.6", {"start": v(508, -3.17) * mm, "mid": v(507.07, -0.93) * mm, "end": v(504.83, 0) * mm});
            skLineSegment(sketch, "E150.0.7", {"start": v(504.83, 0) * mm, "end": v(488.95, 0) * mm});
            skLineSegment(sketch, "E150.0.8", {"start": v(488.95, 0) * mm, "end": v(488.95, -23.81) * mm});
            skSolve(sketch);
        }
        {
            var Q0;
            Q0=makeQuery(id+"F50.imprint","IMPRINT",FACE,{"disambiguationData":[TD([[makeQuery(id+"F50.imprint","IMPRINT",EDGE,{"derivedFrom":sQuery(id+"F50.wireOp",EDGE,"E150.0.0")}),1.0]])]});
            extrude(context, id + "F51", {"entities" : qUnion([Q0]), "endBound" : BoundingType.UP_TO_NEXT, "depth" : 25.4 * mm, "offsetDistance" : 25.4 * mm, "hasSecondDirection" : true, "secondDirectionBound" : BoundingType.UP_TO_NEXT, "secondDirectionOppositeDirection" : true, "secondDirectionDepth" : 25.4 * mm});
        }
    });
